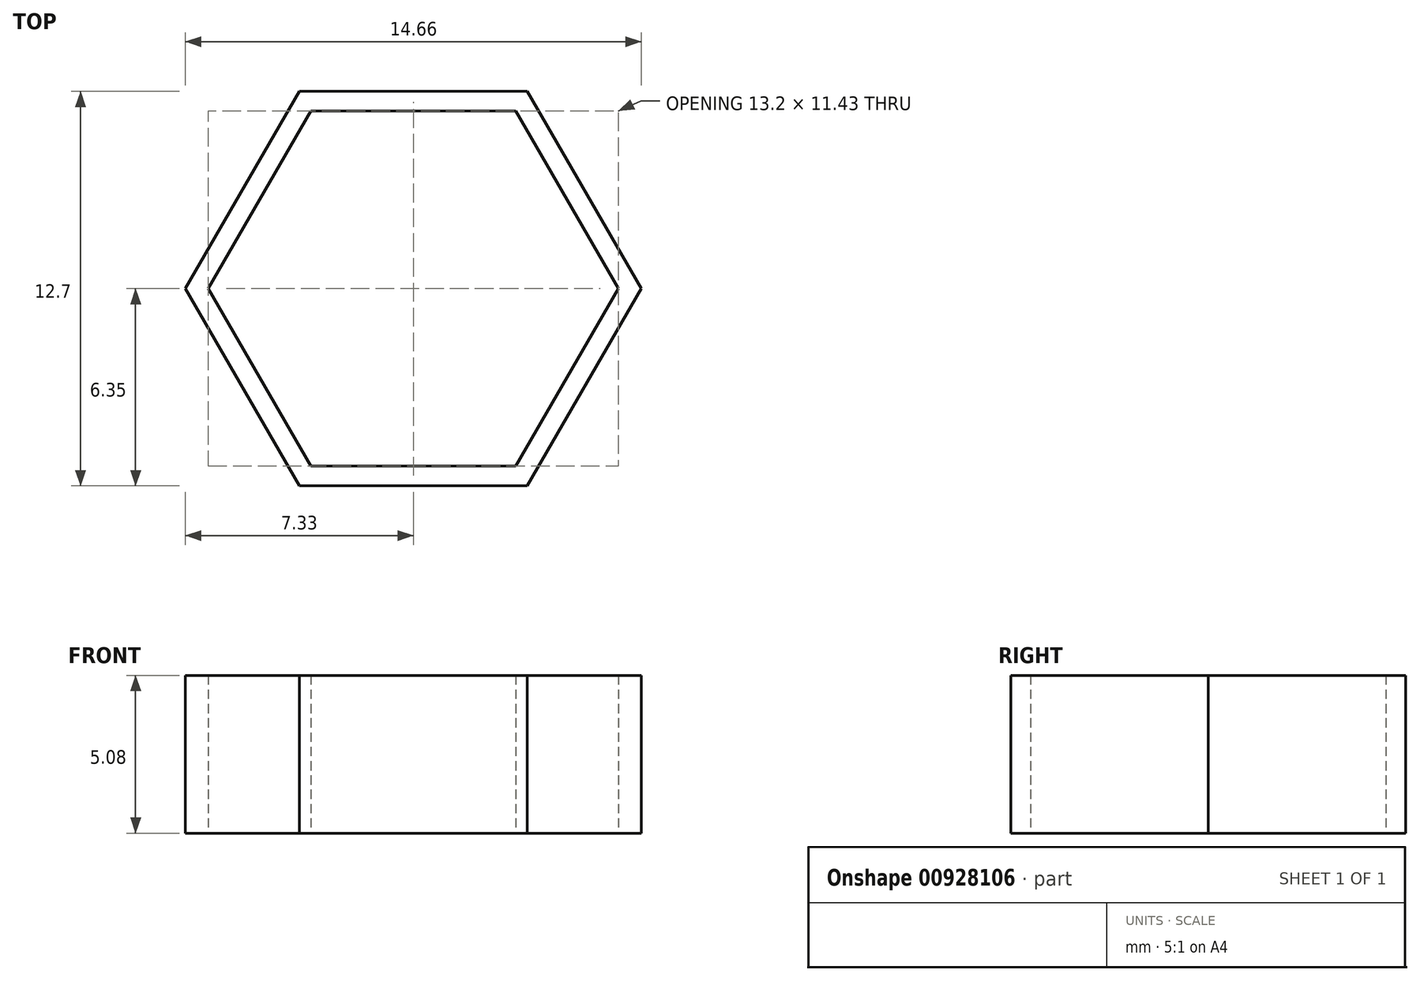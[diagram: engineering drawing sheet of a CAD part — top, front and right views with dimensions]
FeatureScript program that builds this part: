
annotation { "Feature Type Name" : "Feature", "Feature Type Description" : "" }
export const myFeature = defineFeature(function(context is Context, id is Id, definition is map)
    precondition{}
    {
        {
            var Q0;
            Q0=qCreatedBy(makeId("Top.planeOp"),FACE);
            var sketch = newSketch(context, id + "F0", { "sketchPlane" : qUnion([Q0])});
            skCircle(sketch, "E0.cCircle", {"center": v(0, 0) * mm, "radius": 5.72 * mm, "construction": true});
            skLineSegment(sketch, "E0.0", {"start": v(-3.3, 5.72) * mm, "end": v(3.3, 5.72) * mm});
            skLineSegment(sketch, "E0.1", {"start": v(3.3, 5.72) * mm, "end": v(6.6, 0) * mm});
            skLineSegment(sketch, "E0.2", {"start": v(6.6, 0) * mm, "end": v(3.3, -5.72) * mm});
            skLineSegment(sketch, "E0.3", {"start": v(3.3, -5.72) * mm, "end": v(-3.3, -5.72) * mm});
            skLineSegment(sketch, "E0.4", {"start": v(-3.3, -5.72) * mm, "end": v(-6.6, 0) * mm});
            skLineSegment(sketch, "E0.5", {"start": v(-6.6, 0) * mm, "end": v(-3.3, 5.72) * mm});
            skPoint(sketch, "E0.0.midPoint", {"position": v(0, 5.72) * mm});
            skCircle(sketch, "E1.cCircle", {"center": v(0, 0) * mm, "radius": 6.35 * mm, "construction": true});
            skLineSegment(sketch, "E1.0", {"start": v(-3.67, 6.35) * mm, "end": v(3.67, 6.35) * mm});
            skLineSegment(sketch, "E1.1", {"start": v(3.67, 6.35) * mm, "end": v(7.33, 0) * mm});
            skLineSegment(sketch, "E1.2", {"start": v(7.33, 0) * mm, "end": v(3.67, -6.35) * mm});
            skLineSegment(sketch, "E1.3", {"start": v(3.67, -6.35) * mm, "end": v(-3.67, -6.35) * mm});
            skLineSegment(sketch, "E1.4", {"start": v(-3.67, -6.35) * mm, "end": v(-7.33, 0) * mm});
            skLineSegment(sketch, "E1.5", {"start": v(-7.33, 0) * mm, "end": v(-3.67, 6.35) * mm});
            skPoint(sketch, "E1.0.midPoint", {"position": v(0, 6.35) * mm});
            skSolve(sketch);
        }
        {
            var Q0;
            Q0 = qSketchRegion(id + "F0", true);
            extrude(context, id + "F1", {"entities" : qUnion([Q0]), "depth" : 5.08 * mm, "offsetDistance" : 25.4 * mm});
        }
    });
